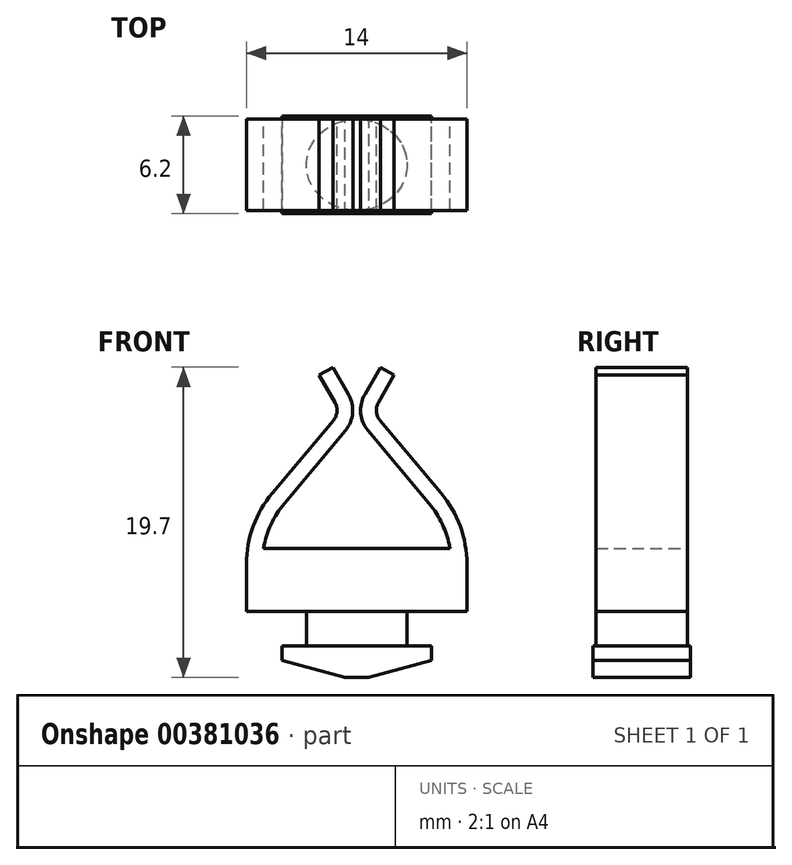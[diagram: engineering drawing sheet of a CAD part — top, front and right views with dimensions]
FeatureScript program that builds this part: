
annotation { "Feature Type Name" : "Feature", "Feature Type Description" : "" }
export const myFeature = defineFeature(function(context is Context, id is Id, definition is map)
    precondition{}
    {
        {
            var Q0;
            Q0=qCreatedBy(makeId("Front.planeOp"),FACE);
            var sketch = newSketch(context, id + "F0", { "sketchPlane" : qUnion([Q0])});
            skLineSegment(sketch, "E0.bottom", {"start": v(-7, 3) * mm, "end": v(7, 3) * mm});
            skLineSegment(sketch, "E0.top", {"start": v(-7, 0) * mm, "end": v(7, 0) * mm});
            skLineSegment(sketch, "E0.left", {"start": v(-7, 3) * mm, "end": v(-7, 0) * mm});
            skLineSegment(sketch, "E0.right", {"start": v(7, 3) * mm, "end": v(7, 0) * mm});
            skSolve(sketch);
        }
        {
            var Q0;
            Q0=qSketchRegion(id+"F0",true);
            extrude(context, id + "F1", {"entities" : qUnion([Q0]), "endBound" : BoundingType.SYMMETRIC, "depth" : 5.8 * mm});
        }
        {
            var Q0;
            Q0=makeQuery(id+"F1.opExtrude","SWEPT_FACE",FACE,{"disambiguationData":[OSD([sQuery(id+"F0.wireOp",EDGE,"E0.top")])]});
            var sketch = newSketch(context, id + "F2", { "sketchPlane" : qUnion([Q0])});
            skEllipse(sketch, "E1", {"center": v(0, 0) * mm, "majorRadius": 3.2 * mm, "minorRadius": 2.9 * mm, "majorAxis": v(1, 0)});
            skSolve(sketch);
        }
        {
            var Q0;
            Q0=qSketchRegion(id+"F2",true);
            extrude(context, id + "F3", {"entities" : qUnion([Q0]), "operationType" : NewBodyOperationType.ADD, "depth" : 2.2 * mm});
        }
        {
            var Q0;
            Q0=qCreatedBy(makeId("Front.planeOp"),FACE);
            var sketch = newSketch(context, id + "F4", { "sketchPlane" : qUnion([Q0])});
            skLineSegment(sketch, "E2.bottom", {"start": v(-4.75, -2.2) * mm, "end": v(4.75, -2.2) * mm});
            skLineSegment(sketch, "E2.top", {"start": v(-4.75, -4.2) * mm, "end": v(4.75, -4.2) * mm});
            skLineSegment(sketch, "E2.left", {"start": v(-4.75, -2.2) * mm, "end": v(-4.75, -4.2) * mm});
            skLineSegment(sketch, "E2.right", {"start": v(4.75, -2.2) * mm, "end": v(4.75, -4.2) * mm});
            skPoint(sketch, "E3", {"position": v(0, -2.2) * mm});
            skSolve(sketch);
        }
        {
            var Q0;
            Q0=makeQuery(id+"F4.imprint","IMPRINT",FACE,{"disambiguationData":[TD([[makeQuery(id+"F4.imprint","IMPRINT",EDGE,{"derivedFrom":sQuery(id+"F4.wireOp",EDGE,"E2.bottom")}),-1.0]])]});
            extrude(context, id + "F5", {"entities" : qUnion([Q0]), "operationType" : NewBodyOperationType.ADD, "endBound" : BoundingType.SYMMETRIC, "depth" : 6.2 * mm});
        }
        {
            var Q0;
            Q0=makeQuery(id+"F5.opExtrude","SWEPT_EDGE",EDGE,{"disambiguationData":[OSD([sQuery(id+"F4.wireOp",EDGE,"E2.top"),sQuery(id+"F4.wireOp",EDGE,"E2.right")])]});
            var Q1;
            Q1=makeQuery(id+"F5.opExtrude","SWEPT_EDGE",EDGE,{"disambiguationData":[OSD([sQuery(id+"F4.wireOp",EDGE,"E2.top"),sQuery(id+"F4.wireOp",EDGE,"E2.left")])]});
            chamfer(context, id + "F6", {"entities" : qUnion([Q0, Q1]), "chamferType" : ChamferType.OFFSET_ANGLE, "width" : 4 * mm, "oppositeDirection" : true, "angle" : 15 * degree, "tangentPropagation" : true});
        }
        {
            var Q0;
            Q0=qCreatedBy(makeId("Front.planeOp"),FACE);
            var sketch = newSketch(context, id + "F7", { "sketchPlane" : qUnion([Q0])});
            skArc(sketch, "E4", {"start": v(7, 3) * mm, "mid": v(6.58, 5.4) * mm, "end": v(5.36, 7.5) * mm});
            skLineSegment(sketch, "E5.0", {"start": v(-7, 3) * mm, "end": v(7, 3) * mm});
            skLineSegment(sketch, "E6", {"start": v(-5.36, 7.5) * mm, "end": v(-1.48, 12.12) * mm});
            skLineSegment(sketch, "E7", {"start": v(0, 3) * mm, "end": v(0, 11.65) * mm, "construction": true});
            skLineSegment(sketch, "E8.MirrorCS", {"start": v(5.36, 7.5) * mm, "end": v(1.48, 12.12) * mm});
            skArc(sketch, "E9", {"start": v(1.48, 12.12) * mm, "mid": v(1.25, 12.68) * mm, "end": v(1.38, 13.26) * mm});
            skLineSegment(sketch, "E10", {"start": v(1.38, 13.26) * mm, "end": v(2.38, 15) * mm});
            skArc(sketch, "E11.MirrorCS", {"start": v(-1.48, 12.12) * mm, "mid": v(-1.25, 12.68) * mm, "end": v(-1.38, 13.26) * mm});
            skLineSegment(sketch, "E12.MirrorCS", {"start": v(-1.38, 13.26) * mm, "end": v(-2.38, 15) * mm});
            skArc(sketch, "E13.trimOffspring", {"start": v(-5.36, 7.5) * mm, "mid": v(-6.58, 5.4) * mm, "end": v(-7, 3) * mm});
            skLineSegment(sketch, "E14.0", {"start": v(-0.52, 13.76) * mm, "end": v(-1.52, 15.5) * mm});
            skArc(sketch, "E14.1", {"start": v(-0.72, 11.48) * mm, "mid": v(-0.26, 12.6) * mm, "end": v(-0.52, 13.76) * mm});
            skLineSegment(sketch, "E14.2", {"start": v(-4.6, 6.86) * mm, "end": v(-0.72, 11.48) * mm});
            skArc(sketch, "E14.3", {"start": v(-4.6, 6.86) * mm, "mid": v(-5.45, 5.52) * mm, "end": v(-5.92, 4) * mm});
            skLineSegment(sketch, "E14.4", {"start": v(-5.92, 4) * mm, "end": v(5.92, 4) * mm});
            skLineSegment(sketch, "E14.5", {"start": v(0.52, 13.76) * mm, "end": v(1.52, 15.5) * mm});
            skArc(sketch, "E14.6", {"start": v(0.72, 11.48) * mm, "mid": v(0.26, 12.6) * mm, "end": v(0.52, 13.76) * mm});
            skLineSegment(sketch, "E14.7", {"start": v(4.6, 6.86) * mm, "end": v(0.72, 11.48) * mm});
            skArc(sketch, "E14.8", {"start": v(5.92, 4) * mm, "mid": v(5.45, 5.52) * mm, "end": v(4.6, 6.86) * mm});
            skLineSegment(sketch, "E15", {"start": v(-2.38, 15) * mm, "end": v(-1.52, 15.5) * mm});
            skLineSegment(sketch, "E16", {"start": v(1.52, 15.5) * mm, "end": v(2.38, 15) * mm});
            skSolve(sketch);
        }
        {
            var Q0;
            Q0 = qSketchRegion(id + "F7", true);
            extrude(context, id + "F8", {"entities" : qUnion([Q0]), "operationType" : NewBodyOperationType.ADD, "endBound" : BoundingType.SYMMETRIC, "depth" : 5.8 * mm});
        }
    });
